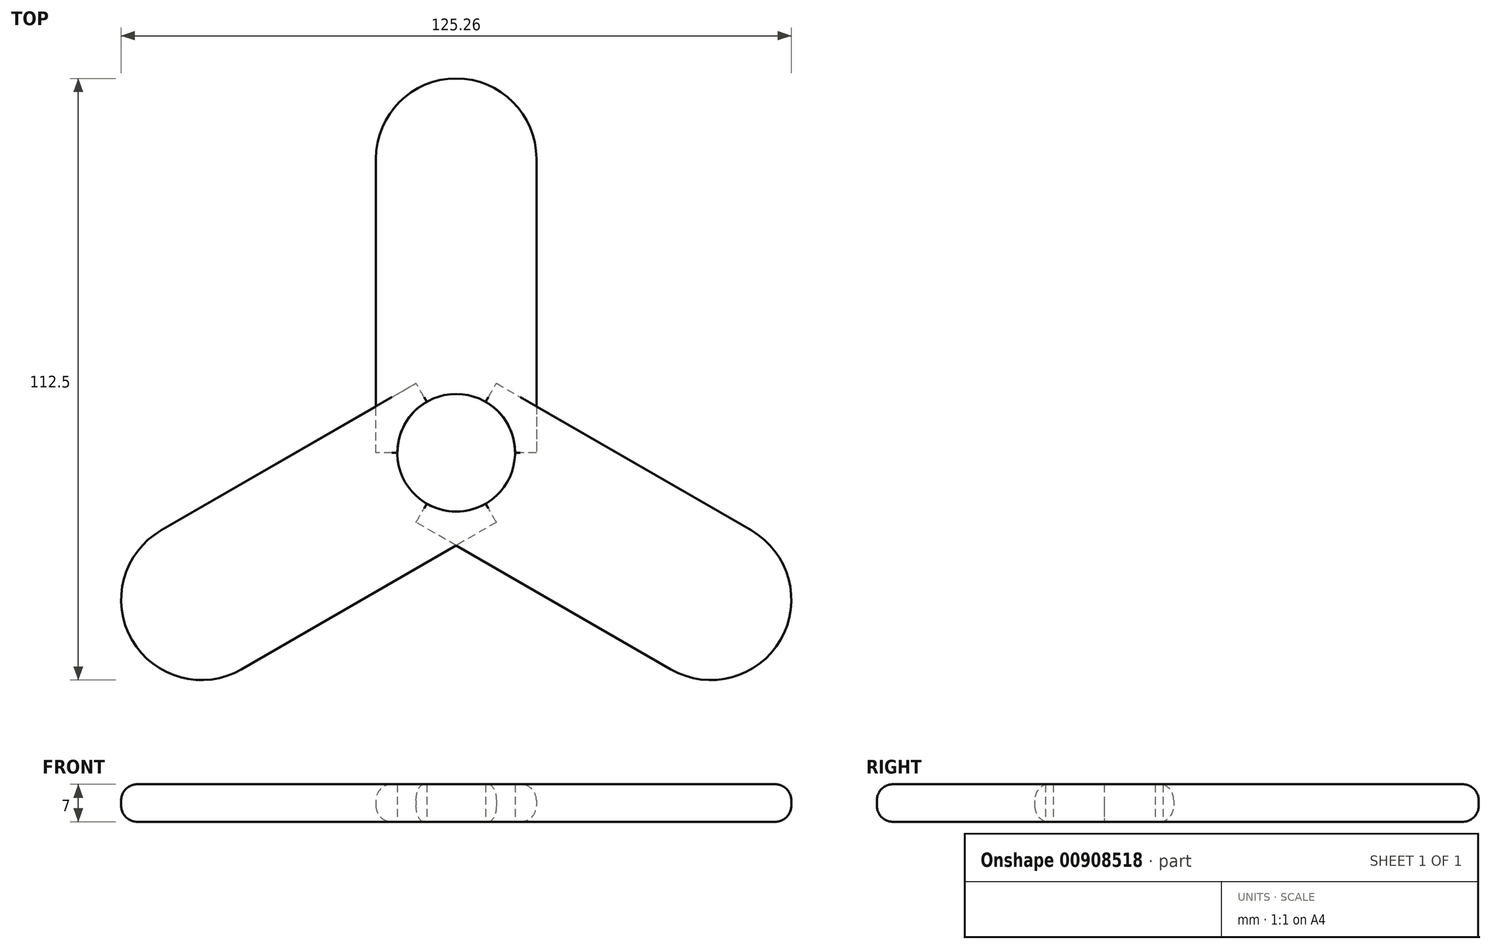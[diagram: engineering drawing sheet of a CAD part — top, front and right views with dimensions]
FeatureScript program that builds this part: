
annotation { "Feature Type Name" : "Feature", "Feature Type Description" : "" }
export const myFeature = defineFeature(function(context is Context, id is Id, definition is map)
    precondition{}
    {
        {
            var Q0;
            Q0=qCreatedBy(makeId("Top.planeOp"),FACE);
            var sketch = newSketch(context, id + "F0", { "sketchPlane" : qUnion([Q0])});
            skCircle(sketch, "E0", {"center": v(0, 0) * mm, "radius": 11 * mm});
            skLineSegment(sketch, "E1", {"start": v(0, 0) * mm, "end": v(0, 70) * mm});
            skLineSegment(sketch, "E2", {"start": v(0, 70) * mm, "end": v(15, 70) * mm});
            skLineSegment(sketch, "E3", {"start": v(15, 70) * mm, "end": v(15, 0) * mm});
            skLineSegment(sketch, "E4", {"start": v(15, 0) * mm, "end": v(0, 0) * mm});
            skLineSegment(sketch, "E5", {"start": v(0, 0) * mm, "end": v(-15, 0) * mm});
            skLineSegment(sketch, "E6", {"start": v(-15, 0) * mm, "end": v(-15, 70) * mm});
            skLineSegment(sketch, "E7", {"start": v(-15, 70) * mm, "end": v(0, 70) * mm});
            skLineSegment(sketch, "E8", {"start": v(0, 70) * mm, "end": v(0, 55) * mm});
            skCircle(sketch, "E9", {"center": v(0, 55) * mm, "radius": 15 * mm});
            skSolve(sketch);
        }
        {
            var Q0;
            {var subQ5=sQuery(id+"F0.wireOp",EDGE,"E1");var subQ6=sQuery(id+"F0.wireOp",EDGE,"E0");var subQ7=makeQuery(id+"F0.imprint","INTERSECT",VERTEX,{"derivedFrom":[subQ6,subQ5]});Q0=makeQuery(id+"F0.imprint","IMPRINT",FACE,{"disambiguationData":[TD([[makeQuery(id+"F0.imprint","IMPRINT",EDGE,{"disambiguationData":[TD([[subQ7,-1.0]])],"derivedFrom":subQ6}),-1.0]])]});}
            var Q1;
            {var subQ1=sQuery(id+"F0.wireOp",EDGE,"E0");var subQ5=sQuery(id+"F0.wireOp",EDGE,"E1");var subQ6=makeQuery(id+"F0.imprint","INTERSECT",VERTEX,{"derivedFrom":[subQ1,subQ5]});Q1=makeQuery(id+"F0.imprint","IMPRINT",FACE,{"disambiguationData":[TD([[makeQuery(id+"F0.imprint","IMPRINT",EDGE,{"disambiguationData":[TD([[subQ6,1.0]])],"derivedFrom":subQ1}),-1.0]])]});}
            var Q2;
            {var subQ0=sQuery(id+"F0.wireOp",EDGE,"E1");var subQ1=makeQuery(id+"F0.imprint","IMPRINT",VERTEX,{"derivedFrom":subQ0});Q2=makeQuery(id+"F0.imprint","IMPRINT",FACE,{"disambiguationData":[TD([[makeQuery(id+"F0.imprint","IMPRINT",EDGE,{"disambiguationData":[TD([[subQ1,1.0]])],"derivedFrom":subQ0}),-1.0]])]});}
            var Q3;
            {var subQ0=sQuery(id+"F0.wireOp",EDGE,"E1");var subQ1=makeQuery(id+"F0.imprint","IMPRINT",VERTEX,{"derivedFrom":subQ0});Q3=makeQuery(id+"F0.imprint","IMPRINT",FACE,{"disambiguationData":[TD([[makeQuery(id+"F0.imprint","IMPRINT",EDGE,{"disambiguationData":[TD([[subQ1,1.0]])],"derivedFrom":subQ0}),1.0]])]});}
            extrude(context, id + "F1", {"entities" : qUnion([Q0, Q1, Q2, Q3]), "depth" : 7 * mm, "offsetDistance" : 25 * mm});
        }
        {
            var Q0;
            Q0=qCreatedBy(makeId("Front.planeOp"),FACE);
            var sketch = newSketch(context, id + "F2", { "sketchPlane" : qUnion([Q0])});
            skLineSegment(sketch, "E10", {"start": v(0, 0) * mm, "end": v(0, 52.28) * mm});
            skSolve(sketch);
        }
        {
            var Q0;
            Q0=makeQuery(id+"F1.opExtrude","SWEPT_BODY",BODY,{"disambiguationData":[OSD([sQuery(id+"F0.wireOp",EDGE,"E0"),sQuery(id+"F0.wireOp",EDGE,"E3"),sQuery(id+"F0.wireOp",EDGE,"E4"),sQuery(id+"F0.wireOp",EDGE,"E5"),sQuery(id+"F0.wireOp",EDGE,"E6"),sQuery(id+"F0.wireOp",EDGE,"E9")])]});
            var Q1;
            Q1=sQuery(id+"F2.wireOp",EDGE,"E10");
            transform(context, id + "F3", {"entities" : qUnion([Q0]), "transformType" : TransformType.ROTATION, "transformAxis" : qUnion([Q1]), "angle" : 120 * degree, "makeCopy" : true});
        }
        {
            var Q0;
            Q0=makeQuery(id+"F1.opExtrude","SWEPT_BODY",BODY,{"disambiguationData":[OSD([sQuery(id+"F0.wireOp",EDGE,"E0"),sQuery(id+"F0.wireOp",EDGE,"E3"),sQuery(id+"F0.wireOp",EDGE,"E4"),sQuery(id+"F0.wireOp",EDGE,"E5"),sQuery(id+"F0.wireOp",EDGE,"E6"),sQuery(id+"F0.wireOp",EDGE,"E9")])]});
            var Q1;
            Q1=sQuery(id+"F2.wireOp",EDGE,"E10");
            transform(context, id + "F4", {"entities" : qUnion([Q0]), "transformType" : TransformType.ROTATION, "transformAxis" : qUnion([Q1]), "angle" : 240 * degree, "makeCopy" : true});
        }
        {
            var Q0;
            Q0=makeQuery(id+"F1.opExtrude","CAP_EDGE",EDGE,{"disambiguationData":[OSD([sQuery(id+"F0.wireOp",EDGE,"E6")])],"isStart":true});
            var Q1;
            Q1=makeQuery(id+"F4.opPattern","COPY",EDGE,{"derivedFrom":makeQuery(id+"F1.opExtrude","CAP_EDGE",EDGE,{"disambiguationData":[OSD([sQuery(id+"F0.wireOp",EDGE,"E3")])],"isStart":true}),"instanceName":"1"});
            var Q2;
            Q2=makeQuery(id+"F3.opPattern","COPY",EDGE,{"derivedFrom":makeQuery(id+"F1.opExtrude","CAP_EDGE",EDGE,{"disambiguationData":[OSD([sQuery(id+"F0.wireOp",EDGE,"E3")])],"isStart":false}),"instanceName":"1"});
            var Q3;
            Q3=makeQuery(id+"F3.opPattern","COPY",EDGE,{"derivedFrom":makeQuery(id+"F1.opExtrude","CAP_EDGE",EDGE,{"disambiguationData":[OSD([sQuery(id+"F0.wireOp",EDGE,"E6")])],"isStart":false}),"instanceName":"1"});
            var Q4;
            Q4=makeQuery(id+"F3.opPattern","COPY",EDGE,{"derivedFrom":makeQuery(id+"F1.opExtrude","CAP_EDGE",EDGE,{"disambiguationData":[OSD([sQuery(id+"F0.wireOp",EDGE,"E6")])],"isStart":true}),"instanceName":"1"});
            var Q5;
            Q5=makeQuery(id+"F4.opPattern","COPY",EDGE,{"derivedFrom":makeQuery(id+"F1.opExtrude","CAP_EDGE",EDGE,{"disambiguationData":[OSD([sQuery(id+"F0.wireOp",EDGE,"E3")])],"isStart":false}),"instanceName":"1"});
            var Q6;
            Q6=makeQuery(id+"F1.opExtrude","CAP_EDGE",EDGE,{"disambiguationData":[OSD([sQuery(id+"F0.wireOp",EDGE,"E3")])],"isStart":false});
            fillet(context, id + "F5", {"entities" : qUnion([Q0, Q1, Q2, Q3, Q4, Q5, Q6]), "radius" : 3 * mm, "tangentPropagation" : true, "allowEdgeOverflow" : false});
        }
    });
